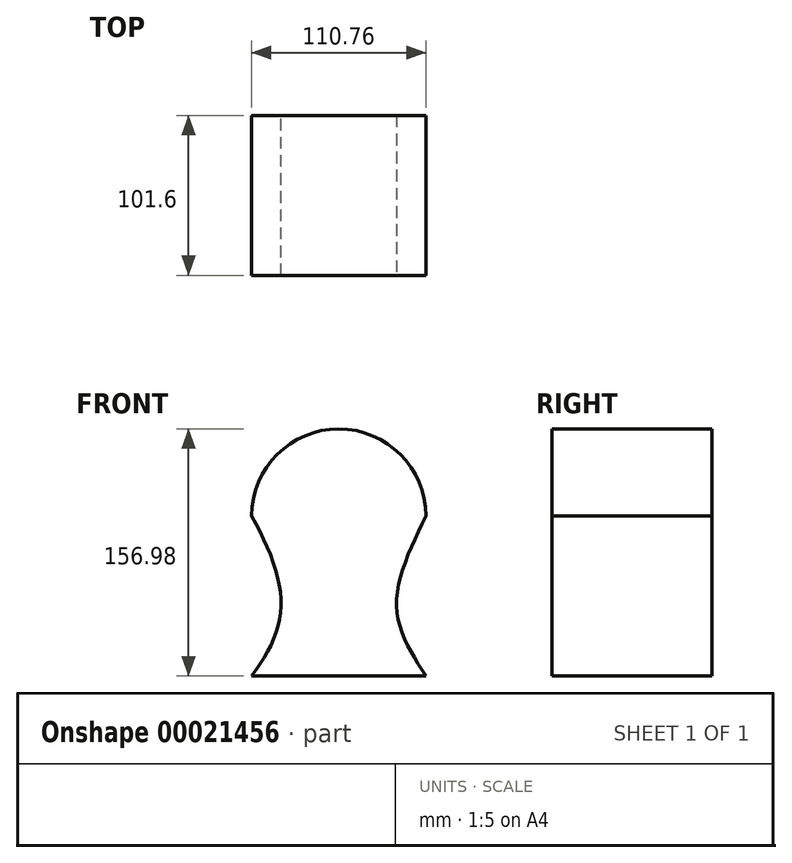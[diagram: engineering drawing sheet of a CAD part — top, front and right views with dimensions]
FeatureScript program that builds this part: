
annotation { "Feature Type Name" : "Feature", "Feature Type Description" : "" }
export const myFeature = defineFeature(function(context is Context, id is Id, definition is map)
    precondition{}
    {
        {
            var Q0;
            Q0=qCreatedBy(makeId("Front.planeOp"),FACE);
            var sketch = newSketch(context, id + "F0", { "sketchPlane" : qUnion([Q0])});
            skPoint(sketch, "E0.center.orphan", {"position": v(0, 130.95) * mm});
            skPoint(sketch, "E1.center.orphan", {"position": v(0, 56.75) * mm});
            skFitSpline(sketch, "E2", {"points": [v(55.38, 0) * mm, v(36.66, -57.92) * mm, v(55.38, -101.6) * mm], "startDerivative": vector(-55.22, -113.34) * mm, "endDerivative": vector(57.54, -89.37) * mm});
            skFitSpline(sketch, "E3", {"points": [v(-55.38, 0) * mm, v(-36.66, -57.92) * mm, v(-55.38, -101.6) * mm], "startDerivative": vector(63.8, -113.7) * mm, "endDerivative": vector(-66.38, -89) * mm});
            skArc(sketch, "E4.trimOffspring", {"start": v(55.38, 0) * mm, "mid": v(0, 55.38) * mm, "end": v(-55.38, 0) * mm});
            skLineSegment(sketch, "E5", {"start": v(-55.38, -101.6) * mm, "end": v(55.38, -101.6) * mm});
            skPoint(sketch, "E6.end.orphan", {"position": v(0, -101.6) * mm});
            skSolve(sketch);
        }
        {
            var Q0;
            Q0 = qSketchRegion(id + "F0", true);
            extrude(context, id + "F1", {"entities" : qUnion([Q0]), "depth" : 88.9 * mm});
        }
        {
            var Q0;
            Q0 = qSketchRegion(id + "F0", true);
            extrude(context, id + "F2", {"entities" : qUnion([Q0]), "operationType" : NewBodyOperationType.ADD, "depth" : 101.6 * mm});
        }
    });
